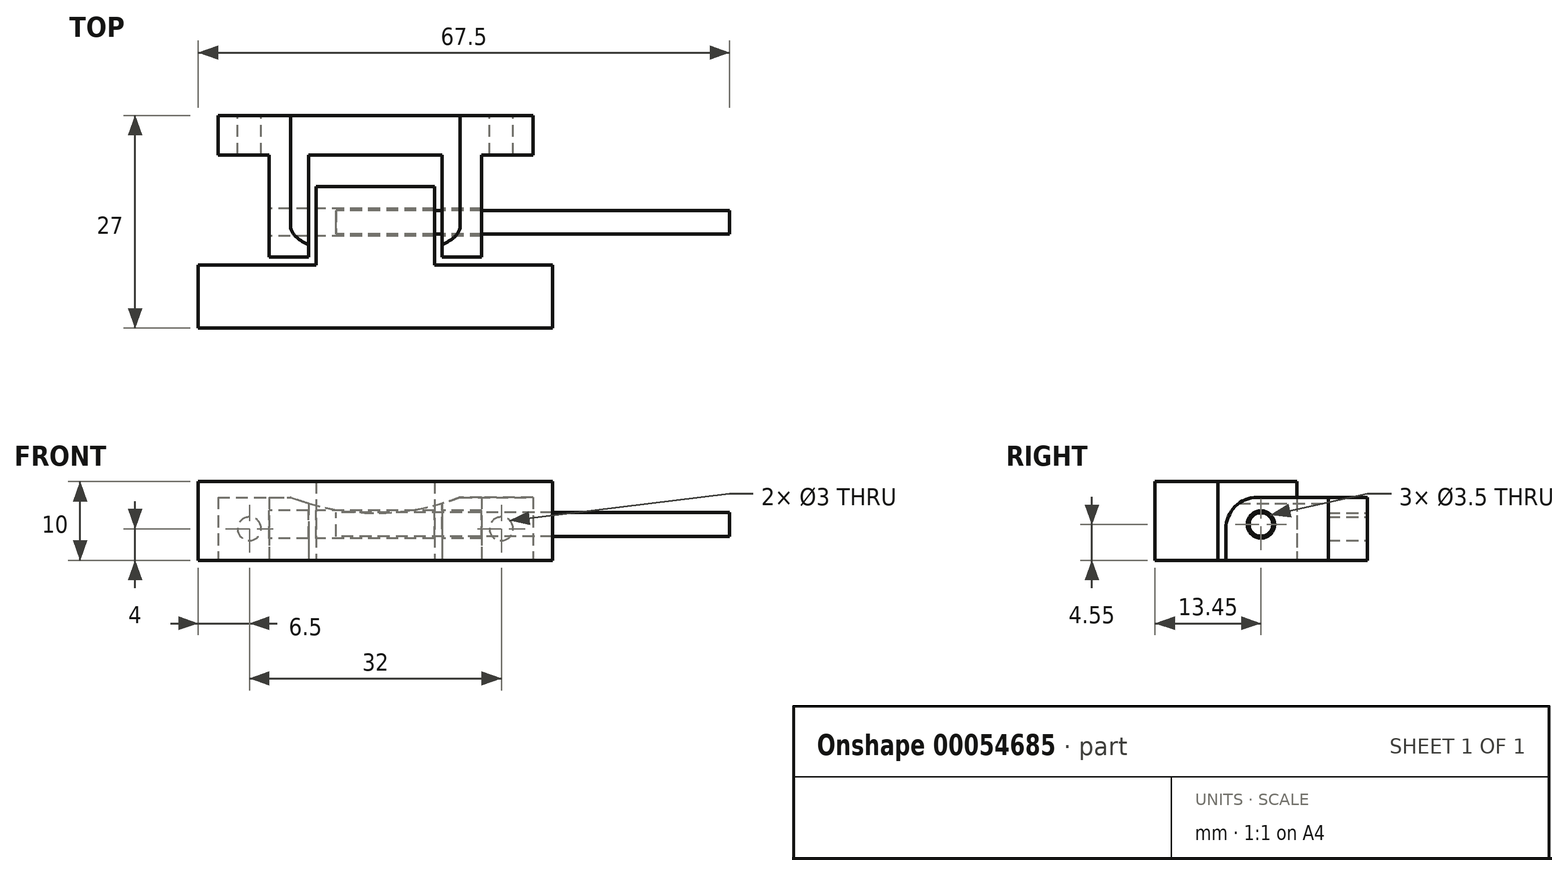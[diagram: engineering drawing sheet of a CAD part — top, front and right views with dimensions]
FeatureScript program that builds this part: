
annotation { "Feature Type Name" : "Feature", "Feature Type Description" : "" }
export const myFeature = defineFeature(function(context is Context, id is Id, definition is map)
    precondition{}
    {
        {
            var Q0;
            Q0=qCreatedBy(makeId("Top.planeOp"),FACE);
            var sketch = newSketch(context, id + "F0", { "sketchPlane" : qUnion([Q0])});
            skLineSegment(sketch, "E0.bottom", {"start": v(0, 0) * mm, "end": v(15, 0) * mm});
            skLineSegment(sketch, "E0.left", {"start": v(0, 0) * mm, "end": v(0, -10) * mm});
            skLineSegment(sketch, "E0.right", {"start": v(15, 0) * mm, "end": v(15, -10) * mm});
            skLineSegment(sketch, "E1.top", {"start": v(-15, -18) * mm, "end": v(30, -18) * mm});
            skLineSegment(sketch, "E1.left", {"start": v(-15, -10) * mm, "end": v(-15, -18) * mm});
            skLineSegment(sketch, "E1.right", {"start": v(30, -10) * mm, "end": v(30, -18) * mm});
            skLineSegment(sketch, "E2", {"start": v(-15, -10) * mm, "end": v(0, -10) * mm});
            skLineSegment(sketch, "E3", {"start": v(15, -10) * mm, "end": v(30, -10) * mm});
            skLineSegment(sketch, "E4.bottom", {"start": v(-12.5, -9) * mm, "end": v(-1, -9) * mm});
            skLineSegment(sketch, "E4.left", {"start": v(-12.5, -9) * mm, "end": v(-12.5, 9) * mm});
            skLineSegment(sketch, "E5", {"start": v(-12.5, 9) * mm, "end": v(27.5, 9) * mm});
            skLineSegment(sketch, "E6", {"start": v(27.5, 9) * mm, "end": v(27.5, -9) * mm});
            skLineSegment(sketch, "E7", {"start": v(27.5, -9) * mm, "end": v(16, -9) * mm});
            skLineSegment(sketch, "E8", {"start": v(16, -9) * mm, "end": v(16, 4) * mm});
            skLineSegment(sketch, "E9", {"start": v(16, 4) * mm, "end": v(-1, 4) * mm});
            skLineSegment(sketch, "E10", {"start": v(-1, 4) * mm, "end": v(-1, -9) * mm});
            skCircle(sketch, "E11", {"center": v(23.5, 5.5) * mm, "radius": 1.5 * mm});
            skCircle(sketch, "E12", {"center": v(-8.5, 5.5) * mm, "radius": 1.5 * mm});
            skLineSegment(sketch, "E13", {"start": v(-12.5, 4) * mm, "end": v(-6, 4) * mm});
            skLineSegment(sketch, "E14", {"start": v(-6, 4) * mm, "end": v(-6, -9) * mm});
            skLineSegment(sketch, "E15", {"start": v(27.5, 4) * mm, "end": v(21, 4) * mm});
            skLineSegment(sketch, "E16", {"start": v(21, 4) * mm, "end": v(21, -9) * mm});
            skSolve(sketch);
        }
        {
            var Q0;
            Q0=makeQuery(id+"F0.imprint","IMPRINT",FACE,{"disambiguationData":[TD([[makeQuery(id+"F0.imprint","IMPRINT",EDGE,{"derivedFrom":sQuery(id+"F0.wireOp",EDGE,"E0.bottom")}),-1.0]])]});
            extrude(context, id + "F1", {"entities" : qUnion([Q0]), "depth" : 10 * mm});
        }
        {
            var Q0;
            {var subQ1=sQuery(id+"F0.wireOp",EDGE,"E5");Q0=makeQuery(id+"F0.imprint","IMPRINT",FACE,{"disambiguationData":[TD([[makeQuery(id+"F0.imprint","IMPRINT",EDGE,{"derivedFrom":subQ1}),-1.0]])]});}
            var Q1;
            Q1=makeQuery(id+"F0.imprint","IMPRINT",FACE,{"disambiguationData":[TD([[makeQuery(id+"F0.imprint","IMPRINT",EDGE,{"derivedFrom":sQuery(id+"F0.wireOp",EDGE,"E12")}),1.0]])]});
            var Q2;
            Q2=makeQuery(id+"F0.imprint","IMPRINT",FACE,{"disambiguationData":[TD([[makeQuery(id+"F0.imprint","IMPRINT",EDGE,{"derivedFrom":sQuery(id+"F0.wireOp",EDGE,"E11")}),1.0]])]});
            extrude(context, id + "F2", {"entities" : qUnion([Q0, Q1, Q2]), "depth" : 8 * mm});
        }
        {
            var Q0;
            Q0=makeQuery(id+"F1.opExtrude","SWEPT_FACE",FACE,{"disambiguationData":[OSD([sQuery(id+"F0.wireOp",EDGE,"E0.left")])]});
            var sketch = newSketch(context, id + "F3", { "sketchPlane" : qUnion([Q0])});
            skCircle(sketch, "E17", {"center": v(4.55, 4.55) * mm, "radius": 1.75 * mm});
            skSolve(sketch);
        }
        {
            var Q0;
            Q0=qSketchRegion(id+"F3",true);
            extrude(context, id + "F4", {"entities" : qUnion([Q0]), "operationType" : NewBodyOperationType.REMOVE, "endBound" : BoundingType.SYMMETRIC, "oppositeDirection" : true, "depth" : 100 * mm});
        }
        {
            var Q0;
            Q0=makeQuery(id+"F2.opExtrude","SWEPT_FACE",FACE,{"disambiguationData":[OSD([sQuery(id+"F0.wireOp",EDGE,"E6")])]});
            var sketch = newSketch(context, id + "F5", { "sketchPlane" : qUnion([Q0])});
            skCircle(sketch, "E18", {"center": v(-4.55, 4.55) * mm, "radius": 1.5 * mm});
            skSolve(sketch);
        }
        {
            var Q0;
            Q0=qSketchRegion(id+"F5",true);
            extrude(context, id + "F6", {"entities" : qUnion([Q0]), "endBound" : BoundingType.SYMMETRIC, "depth" : 50 * mm});
        }
        {
            var Q0;
            Q0=makeQuery(id+"F0.imprint","IMPRINT",FACE,{"disambiguationData":[TD([[makeQuery(id+"F0.imprint","IMPRINT",EDGE,{"derivedFrom":sQuery(id+"F0.wireOp",EDGE,"E4.bottom")}),1.0]])]});
            extrude(context, id + "F7", {"entities" : qUnion([Q0]), "operationType" : NewBodyOperationType.REMOVE, "depth" : 1 * mm});
        }
        {
            var Q0;
            Q0=makeQuery(id+"F2.opExtrude","CAP_EDGE",EDGE,{"disambiguationData":[OSD([sQuery(id+"F0.wireOp",EDGE,"E7")])],"isStart":false});
            var Q1;
            Q1=makeQuery(id+"F2.opExtrude","CAP_EDGE",EDGE,{"disambiguationData":[OSD([sQuery(id+"F0.wireOp",EDGE,"E4.bottom")])],"isStart":false});
            fillet(context, id + "F8", {"entities" : qUnion([Q0, Q1]), "radius" : 4 * mm, "tangentPropagation" : true, "allowEdgeOverflow" : false});
        }
        {
            var Q0;
            Q0=makeQuery(id+"F2.opExtrude","SWEPT_FACE",FACE,{"disambiguationData":[OSD([sQuery(id+"F0.wireOp",EDGE,"E5")])]});
            var sketch = newSketch(context, id + "F9", { "sketchPlane" : qUnion([Q0])});
            skCircle(sketch, "E19", {"center": v(8.5, 4) * mm, "radius": 1.5 * mm});
            skCircle(sketch, "E20", {"center": v(-23.5, 4) * mm, "radius": 1.5 * mm});
            skArc(sketch, "E21", {"start": v(-18.27, 8) * mm, "mid": v(-7.5, 6) * mm, "end": v(3.27, 8) * mm});
            skLineSegment(sketch, "E22", {"start": v(-18.27, 8) * mm, "end": v(-27.5, 8) * mm, "construction": true});
            skLineSegment(sketch, "E23", {"start": v(3.27, 8) * mm, "end": v(12.5, 8) * mm, "construction": true});
            skSolve(sketch);
        }
        {
            var Q0;
            Q0 = qSketchRegion(id + "F9", true);
            var Q1;
            {var subQ0=sQuery(id+"F9.wireOp",EDGE,"E21");Q1=makeQuery(id+"F9.imprint","IMPRINT",FACE,{"disambiguationData":[TD([[makeQuery(id+"F9.imprint","IMPRINT",EDGE,{"derivedFrom":subQ0}),1.0]])]});}
            extrude(context, id + "F10", {"entities" : qUnion([Q0, Q1]), "operationType" : NewBodyOperationType.REMOVE, "endBound" : BoundingType.UP_TO_NEXT, "oppositeDirection" : true, "depth" : 25 * mm});
        }
    });
